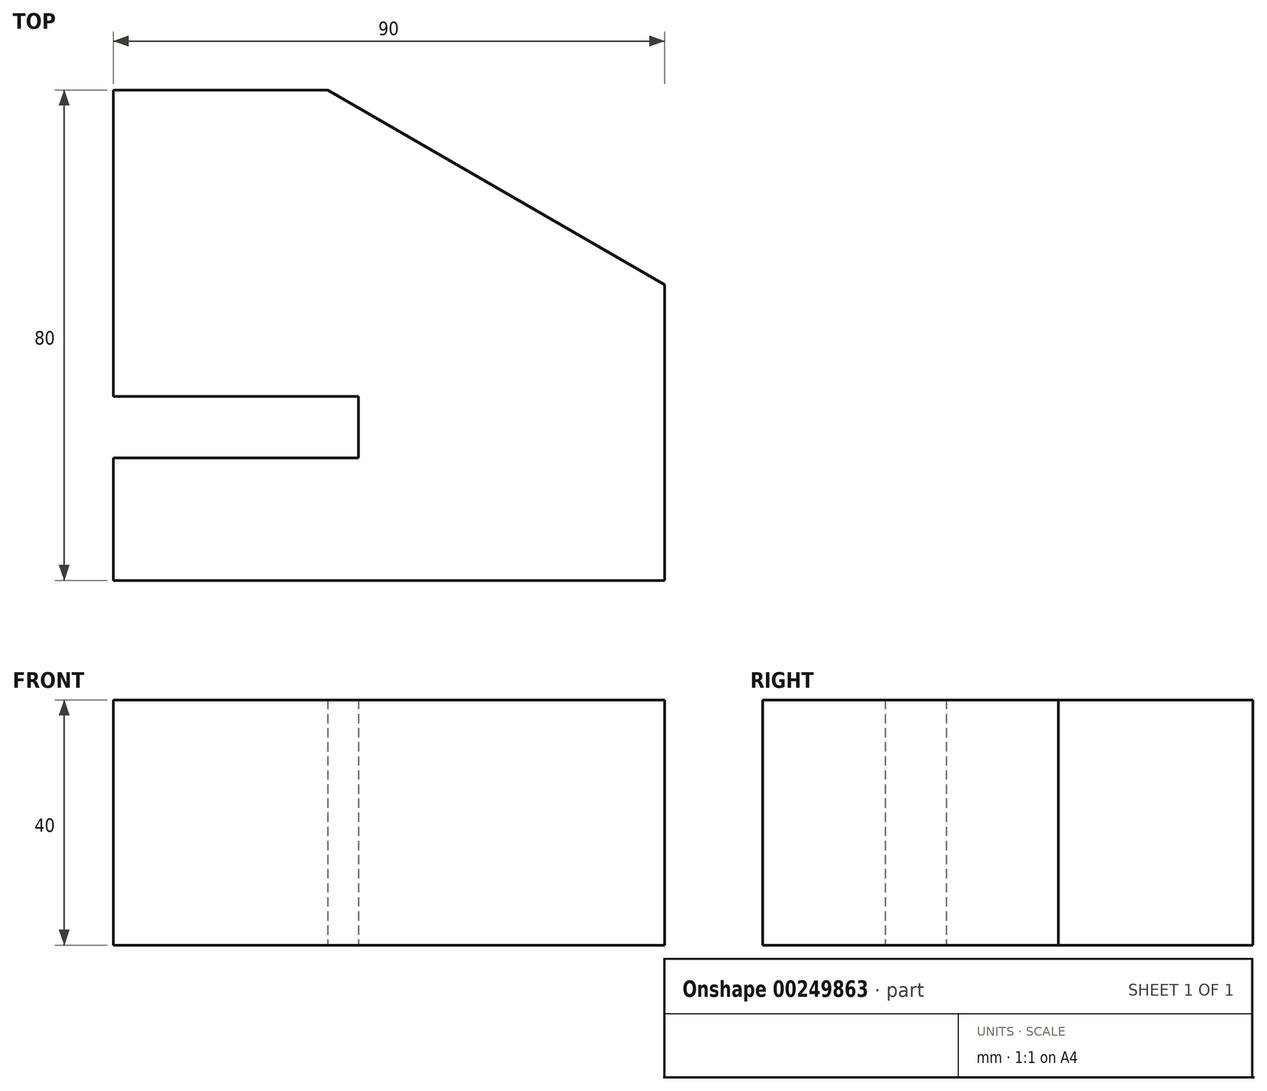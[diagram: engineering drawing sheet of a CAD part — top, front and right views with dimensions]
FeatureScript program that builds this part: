
annotation { "Feature Type Name" : "Feature", "Feature Type Description" : "" }
export const myFeature = defineFeature(function(context is Context, id is Id, definition is map)
    precondition{}
    {
        {
            var Q0;
            Q0=qCreatedBy(makeId("Top.planeOp"),FACE);
            var sketch = newSketch(context, id + "F0", { "sketchPlane" : qUnion([Q0])});
            skLineSegment(sketch, "E0", {"start": v(-40, 0) * mm, "end": v(-40, -20) * mm});
            skLineSegment(sketch, "E1", {"start": v(-40, -20) * mm, "end": v(50, -20) * mm});
            skLineSegment(sketch, "E2", {"start": v(50, -20) * mm, "end": v(50, 28.25) * mm});
            skLineSegment(sketch, "E3", {"start": v(50, 28.25) * mm, "end": v(-5, 60) * mm});
            skLineSegment(sketch, "E4", {"start": v(-5, 60) * mm, "end": v(-40, 60) * mm});
            skLineSegment(sketch, "E5", {"start": v(-40, 60) * mm, "end": v(-40, 10) * mm});
            skLineSegment(sketch, "E6", {"start": v(-40, 10) * mm, "end": v(0, 10) * mm});
            skLineSegment(sketch, "E7", {"start": v(0, 10) * mm, "end": v(0, 0) * mm});
            skLineSegment(sketch, "E8", {"start": v(0, 0) * mm, "end": v(-40, 0) * mm});
            skSolve(sketch);
        }
        {
            var Q0;
            Q0 = qSketchRegion(id + "F0", true);
            extrude(context, id + "F1", {"entities" : qUnion([Q0]), "depth" : 40 * mm});
        }
    });
